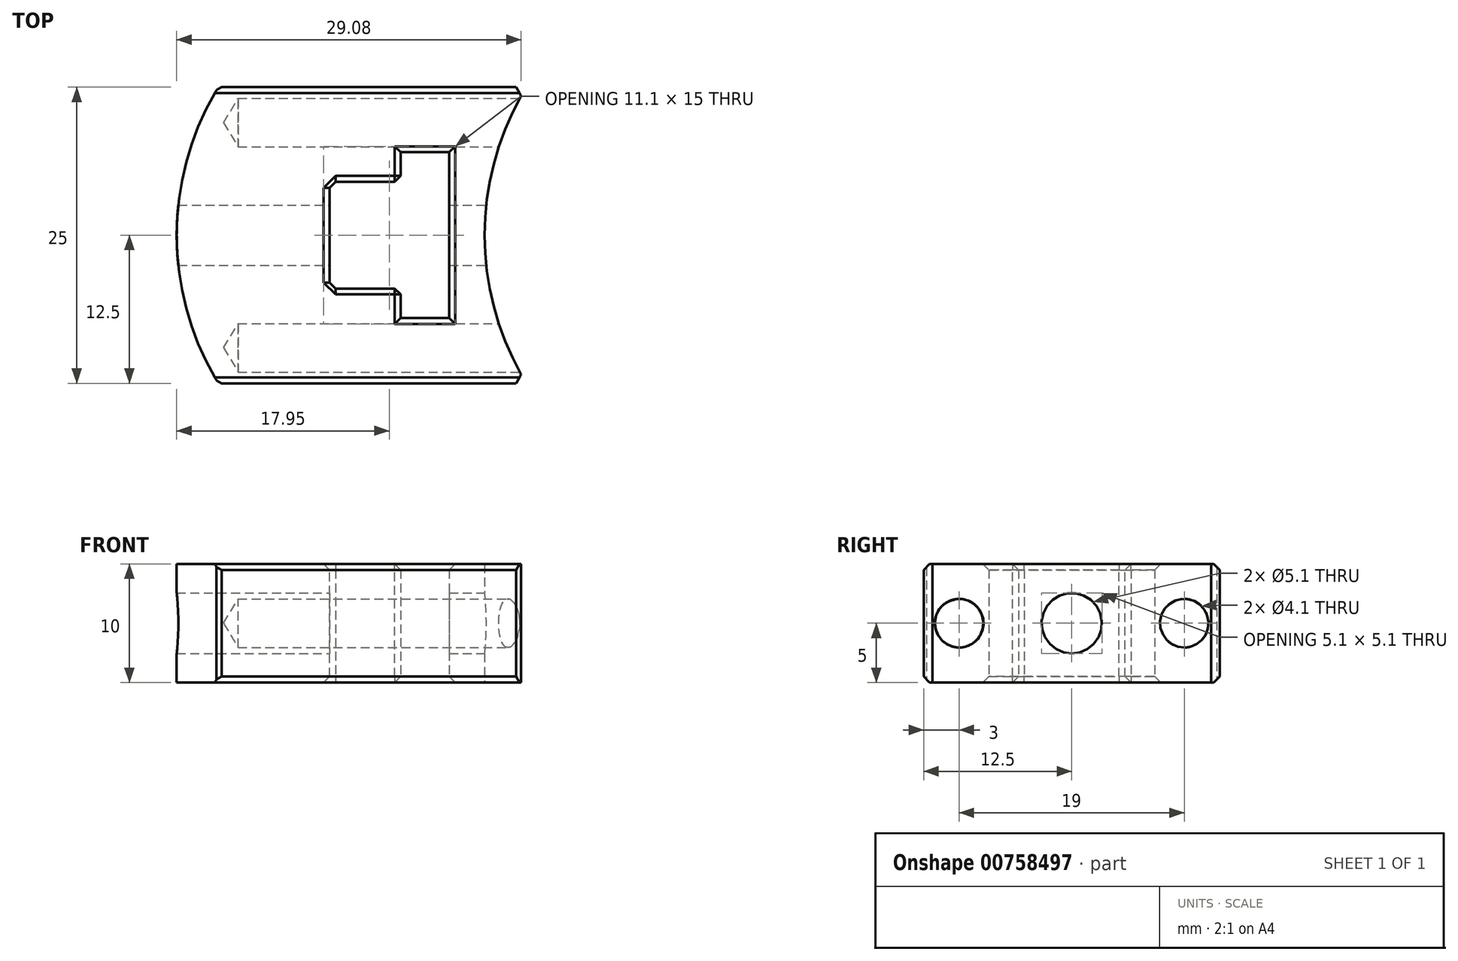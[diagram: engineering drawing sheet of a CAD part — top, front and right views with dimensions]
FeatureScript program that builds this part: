
annotation { "Feature Type Name" : "Feature", "Feature Type Description" : "" }
export const myFeature = defineFeature(function(context is Context, id is Id, definition is map)
    precondition{}
    {
        {
            var Q0;
            Q0=qCreatedBy(makeId("Top.planeOp"),FACE);
            var sketch = newSketch(context, id + "F0", { "sketchPlane" : qUnion([Q0])});
            skCircle(sketch, "E0", {"center": v(0, 0) * mm, "radius": 24 * mm});
            skLineSegment(sketch, "E1.bottom", {"start": v(20.49, 12.5) * mm, "end": v(-20.49, 12.5) * mm});
            skLineSegment(sketch, "E1.top", {"start": v(20.49, -12.5) * mm, "end": v(-20.49, -12.5) * mm});
            skLineSegment(sketch, "E1.left", {"start": v(20.49, 12.5) * mm, "end": v(20.49, -12.5) * mm});
            skLineSegment(sketch, "E1.right", {"start": v(-20.49, 12.5) * mm, "end": v(-20.49, -12.5) * mm});
            skCircle(sketch, "E2", {"center": v(26, 0) * mm, "radius": 24 * mm});
            skPoint(sketch, "E3", {"position": v(20.49, 0) * mm});
            skLineSegment(sketch, "E4.bottom", {"start": v(-5.1, -7) * mm, "end": v(-1, -7) * mm});
            skLineSegment(sketch, "E4.top", {"start": v(-5.1, 7) * mm, "end": v(-1, 7) * mm});
            skLineSegment(sketch, "E4.left", {"start": v(-5.1, -7) * mm, "end": v(-5.1, 7) * mm});
            skLineSegment(sketch, "E4.right", {"start": v(-1, -7) * mm, "end": v(-1, 7) * mm});
            skPoint(sketch, "E4.middle", {"position": v(-3.05, 0) * mm});
            skLineSegment(sketch, "E5.bottom", {"start": v(-5.1, -4.5) * mm, "end": v(-11.1, -4.5) * mm});
            skLineSegment(sketch, "E5.top", {"start": v(-5.1, 4.5) * mm, "end": v(-11.1, 4.5) * mm});
            skLineSegment(sketch, "E5.left", {"start": v(-5.1, -4.5) * mm, "end": v(-5.1, 4.5) * mm});
            skLineSegment(sketch, "E5.right", {"start": v(-11.1, -4.5) * mm, "end": v(-11.1, 4.5) * mm});
            skPoint(sketch, "E5.middle", {"position": v(-8.1, 0) * mm});
            skSolve(sketch);
        }
        {
            var Q0;
            {var subQ0=sQuery(id+"F0.wireOp",EDGE,"E1.right");Q0=makeQuery(id+"F0.imprint","IMPRINT",FACE,{"disambiguationData":[TD([[makeQuery(id+"F0.imprint","IMPRINT",EDGE,{"derivedFrom":subQ0}),1.0]])]});}
            var Q1;
            {var subQ0=sQuery(id+"F0.wireOp",EDGE,"E1.right");Q1=makeQuery(id+"F0.imprint","IMPRINT",FACE,{"disambiguationData":[TD([[makeQuery(id+"F0.imprint","IMPRINT",EDGE,{"derivedFrom":subQ0}),-1.0]])]});}
            extrude(context, id + "F1", {"entities" : qUnion([Q0, Q1]), "depth" : 10 * mm, "offsetDistance" : 25 * mm});
        }
        {
            var Q0;
            Q0=qCreatedBy(makeId("Right.planeOp"),FACE);
            cPlane(context, id + "F2", {"entities" : qUnion([Q0]), "cplaneType" : CPlaneType.OFFSET, "offset" : 30 * mm, "width" : 150 * mm, "height" : 150 * mm});
        }
        {
            var Q0;
            Q0=qCreatedBy(id+"F2.planeOp",FACE);
            var sketch = newSketch(context, id + "F3", { "sketchPlane" : qUnion([Q0])});
            skPoint(sketch, "E6", {"position": v(0, 5) * mm});
            skPoint(sketch, "E7", {"position": v(9.5, 5) * mm});
            skPoint(sketch, "E8.MirrorP", {"position": v(-9.5, 5) * mm});
            skSolve(sketch);
        }
        {
            var Q0;
            Q0=sQuery(id+"F3.wireOp",VERTEX,"E6");
            var Q1;
            Q1=makeQuery(id+"F1.opExtrude","SWEPT_BODY",BODY,{"disambiguationData":[OSD([sQuery(id+"F0.wireOp",EDGE,"E0"),sQuery(id+"F0.wireOp",EDGE,"E1.bottom"),sQuery(id+"F0.wireOp",EDGE,"E1.top"),sQuery(id+"F0.wireOp",EDGE,"52ejzwmu-p2sd-T4fg-TEem-IFdslxl9ynHk.bottom"),sQuery(id+"F0.wireOp",EDGE,"52ejzwmu-p2sd-T4fg-TEem-IFdslxl9ynHk.top"),sQuery(id+"F0.wireOp",EDGE,"52ejzwmu-p2sd-T4fg-TEem-IFdslxl9ynHk.left"),sQuery(id+"F0.wireOp",EDGE,"52ejzwmu-p2sd-T4fg-TEem-IFdslxl9ynHk.right"),sQuery(id+"F0.wireOp",EDGE,"j2K1zlM2-5mF2-7mnx-XZQx-q8SdQ0DQluRe.bottom"),sQuery(id+"F0.wireOp",EDGE,"j2K1zlM2-5mF2-7mnx-XZQx-q8SdQ0DQluRe.top")])]});
            hole(context, id + "F4", {"style" : HoleStyle.SIMPLE, "endStyle" : HoleEndStyle.THROUGH, "holeDiameter" : 5.1 * mm, "majorDiameter" : 5 * mm, "isTappedThrough" : true, "tappedDepth" : 12 * mm, "tapClearance" : 3, "locations" : qUnion([Q0]), "scope" : qUnion([Q1])});
        }
        {
            var Q0;
            Q0=sQuery(id+"F3.wireOp",VERTEX,"E8.MirrorP");
            var Q1;
            Q1=sQuery(id+"F3.wireOp",VERTEX,"E7");
            var Q2;
            Q2=makeQuery(id+"F1.opExtrude","SWEPT_BODY",BODY,{"disambiguationData":[OSD([sQuery(id+"F0.wireOp",EDGE,"E0"),sQuery(id+"F0.wireOp",EDGE,"E1.bottom"),sQuery(id+"F0.wireOp",EDGE,"E1.top"),sQuery(id+"F0.wireOp",EDGE,"52ejzwmu-p2sd-T4fg-TEem-IFdslxl9ynHk.bottom"),sQuery(id+"F0.wireOp",EDGE,"52ejzwmu-p2sd-T4fg-TEem-IFdslxl9ynHk.top"),sQuery(id+"F0.wireOp",EDGE,"52ejzwmu-p2sd-T4fg-TEem-IFdslxl9ynHk.left"),sQuery(id+"F0.wireOp",EDGE,"52ejzwmu-p2sd-T4fg-TEem-IFdslxl9ynHk.right"),sQuery(id+"F0.wireOp",EDGE,"j2K1zlM2-5mF2-7mnx-XZQx-q8SdQ0DQluRe.bottom"),sQuery(id+"F0.wireOp",EDGE,"j2K1zlM2-5mF2-7mnx-XZQx-q8SdQ0DQluRe.top")])]});
            hole(context, id + "F5", {"style" : HoleStyle.SIMPLE, "endStyle" : HoleEndStyle.BLIND, "holeDiameter" : 4.1 * mm, "majorDiameter" : 5 * mm, "holeDepth" : 22 * mm, "isTappedThrough" : true, "tappedDepth" : 12 * mm, "tapClearance" : 3, "locations" : qUnion([Q0, Q1]), "scope" : qUnion([Q2])});
        }
        {
            var Q0;
            {var subQ0=sQuery(id+"F0.wireOp",EDGE,"j2K1zlM2-5mF2-7mnx-XZQx-q8SdQ0DQluRe.top");Q0=makeQuery(id+"F8zHJOIqJvhwJ6n_1.boolean.opBoolean","MERGE",FACE,{"derivedFrom":[makeQuery(id+"F1.opExtrude","SWEPT_FACE",FACE,{"disambiguationData":[OSD([sQuery(id+"F0.wireOp",EDGE,"E1.top"),subQ0])]}),makeQuery(id+"F8zHJOIqJvhwJ6n_1.opExtrude","SWEPT_FACE",FACE,{"disambiguationData":[OSD([subQ0])]})]});}
            var Q1;
            {var subQ0=sQuery(id+"F0.wireOp",EDGE,"j2K1zlM2-5mF2-7mnx-XZQx-q8SdQ0DQluRe.bottom");Q1=makeQuery(id+"F8zHJOIqJvhwJ6n_1.boolean.opBoolean","MERGE",FACE,{"derivedFrom":[makeQuery(id+"F1.opExtrude","SWEPT_FACE",FACE,{"disambiguationData":[OSD([sQuery(id+"F0.wireOp",EDGE,"E1.bottom"),subQ0])]}),makeQuery(id+"F8zHJOIqJvhwJ6n_1.opExtrude","SWEPT_FACE",FACE,{"disambiguationData":[OSD([subQ0])]})]});}
            var Q2;
            Q2=makeQuery(id+"F8zHJOIqJvhwJ6n_1.opExtrude","CAP_EDGE",EDGE,{"disambiguationData":[OSD([sQuery(id+"F0.wireOp",EDGE,"j2K1zlM2-5mF2-7mnx-XZQx-q8SdQ0DQluRe.right")])],"isStart":false});
            var Q3;
            Q3=makeQuery(id+"F8zHJOIqJvhwJ6n_1.opExtrude","CAP_EDGE",EDGE,{"disambiguationData":[OSD([sQuery(id+"F0.wireOp",EDGE,"j2K1zlM2-5mF2-7mnx-XZQx-q8SdQ0DQluRe.left")])],"isStart":false});
            chamfer(context, id + "F6", {"entities" : qUnion([Q0, Q1, Q2, Q3]), "width" : 0.5 * mm, "tangentPropagation" : true});
        }
        {
            var Q0;
            Q0=makeQuery(id+"F1.opExtrude","CAP_EDGE",EDGE,{"disambiguationData":[OSD([sQuery(id+"F0.wireOp",EDGE,"E5.right")])],"isStart":true});
            var Q1;
            Q1=makeQuery(id+"F1.opExtrude","CAP_EDGE",EDGE,{"disambiguationData":[OSD([sQuery(id+"F0.wireOp",EDGE,"E5.bottom")])],"isStart":true});
            var Q2;
            Q2=makeQuery(id+"F1.opExtrude","CAP_EDGE",EDGE,{"disambiguationData":[OSD([sQuery(id+"F0.wireOp",EDGE,"E4.bottom")])],"isStart":true});
            var Q3;
            {var subQ0=sQuery(id+"F0.wireOp",EDGE,"E4.left");Q3=makeQuery(id+"F1.opExtrude","CAP_EDGE",EDGE,{"disambiguationData":[OSD([subQ0]),TDD([makeQuery(id+"F0.imprint","IMPRINT",EDGE,{"disambiguationData":[TD([[makeQuery(id+"F0.imprint","INTERSECT",VERTEX,{"derivedFrom":[sQuery(id+"F0.wireOp",EDGE,"E4.bottom"),subQ0]}),-1.0]])],"derivedFrom":subQ0})])],"isStart":true});}
            var Q4;
            Q4=makeQuery(id+"F1.opExtrude","CAP_EDGE",EDGE,{"disambiguationData":[OSD([sQuery(id+"F0.wireOp",EDGE,"E4.right")])],"isStart":true});
            var Q5;
            Q5=makeQuery(id+"F1.opExtrude","CAP_EDGE",EDGE,{"disambiguationData":[OSD([sQuery(id+"F0.wireOp",EDGE,"E4.top")])],"isStart":true});
            var Q6;
            {var subQ0=sQuery(id+"F0.wireOp",EDGE,"E4.left");Q6=makeQuery(id+"F1.opExtrude","CAP_EDGE",EDGE,{"disambiguationData":[OSD([subQ0]),TDD([makeQuery(id+"F0.imprint","IMPRINT",EDGE,{"disambiguationData":[TD([[makeQuery(id+"F0.imprint","INTERSECT",VERTEX,{"derivedFrom":[sQuery(id+"F0.wireOp",EDGE,"E4.top"),subQ0]}),1.0]])],"derivedFrom":subQ0})])],"isStart":true});}
            var Q7;
            Q7=makeQuery(id+"F1.opExtrude","CAP_EDGE",EDGE,{"disambiguationData":[OSD([sQuery(id+"F0.wireOp",EDGE,"E5.top")])],"isStart":true});
            var Q8;
            Q8=makeQuery(id+"F1.opExtrude","SWEPT_EDGE",EDGE,{"disambiguationData":[OSD([sQuery(id+"F0.wireOp",EDGE,"E4.left"),sQuery(id+"F0.wireOp",EDGE,"E5.bottom"),sQuery(id+"F0.wireOp",EDGE,"E5.left")])]});
            var Q9;
            Q9=makeQuery(id+"F1.opExtrude","SWEPT_EDGE",EDGE,{"disambiguationData":[OSD([sQuery(id+"F0.wireOp",EDGE,"E4.left"),sQuery(id+"F0.wireOp",EDGE,"E5.top"),sQuery(id+"F0.wireOp",EDGE,"E5.left")])]});
            var Q10;
            Q10=makeQuery(id+"F1.opExtrude","SWEPT_EDGE",EDGE,{"disambiguationData":[OSD([sQuery(id+"F0.wireOp",EDGE,"E5.top"),sQuery(id+"F0.wireOp",EDGE,"E5.right")])]});
            var Q11;
            Q11=makeQuery(id+"F1.opExtrude","SWEPT_EDGE",EDGE,{"disambiguationData":[OSD([sQuery(id+"F0.wireOp",EDGE,"E5.bottom"),sQuery(id+"F0.wireOp",EDGE,"E5.right")])]});
            var Q12;
            Q12=makeQuery(id+"F1.opExtrude","CAP_EDGE",EDGE,{"disambiguationData":[OSD([sQuery(id+"F0.wireOp",EDGE,"E4.right")])],"isStart":false});
            var Q13;
            Q13=makeQuery(id+"F1.opExtrude","CAP_EDGE",EDGE,{"disambiguationData":[OSD([sQuery(id+"F0.wireOp",EDGE,"E4.bottom")])],"isStart":false});
            var Q14;
            {var subQ0=sQuery(id+"F0.wireOp",EDGE,"E4.left");Q14=makeQuery(id+"F1.opExtrude","CAP_EDGE",EDGE,{"disambiguationData":[OSD([subQ0]),TDD([makeQuery(id+"F0.imprint","IMPRINT",EDGE,{"disambiguationData":[TD([[makeQuery(id+"F0.imprint","INTERSECT",VERTEX,{"derivedFrom":[sQuery(id+"F0.wireOp",EDGE,"E4.bottom"),subQ0]}),-1.0]])],"derivedFrom":subQ0})])],"isStart":false});}
            var Q15;
            Q15=makeQuery(id+"F1.opExtrude","CAP_EDGE",EDGE,{"disambiguationData":[OSD([sQuery(id+"F0.wireOp",EDGE,"E5.bottom")])],"isStart":false});
            var Q16;
            Q16=makeQuery(id+"F1.opExtrude","CAP_EDGE",EDGE,{"disambiguationData":[OSD([sQuery(id+"F0.wireOp",EDGE,"E4.top")])],"isStart":false});
            var Q17;
            {var subQ0=sQuery(id+"F0.wireOp",EDGE,"E4.left");Q17=makeQuery(id+"F1.opExtrude","CAP_EDGE",EDGE,{"disambiguationData":[OSD([subQ0]),TDD([makeQuery(id+"F0.imprint","IMPRINT",EDGE,{"disambiguationData":[TD([[makeQuery(id+"F0.imprint","INTERSECT",VERTEX,{"derivedFrom":[sQuery(id+"F0.wireOp",EDGE,"E4.top"),subQ0]}),1.0]])],"derivedFrom":subQ0})])],"isStart":false});}
            chamfer(context, id + "F7", {"entities" : qUnion([Q0, Q1, Q2, Q3, Q4, Q5, Q6, Q7, Q8, Q9, Q10, Q11, Q12, Q13, Q14, Q15, Q16, Q17]), "width" : 0.5 * mm, "tangentPropagation" : true});
        }
    });
